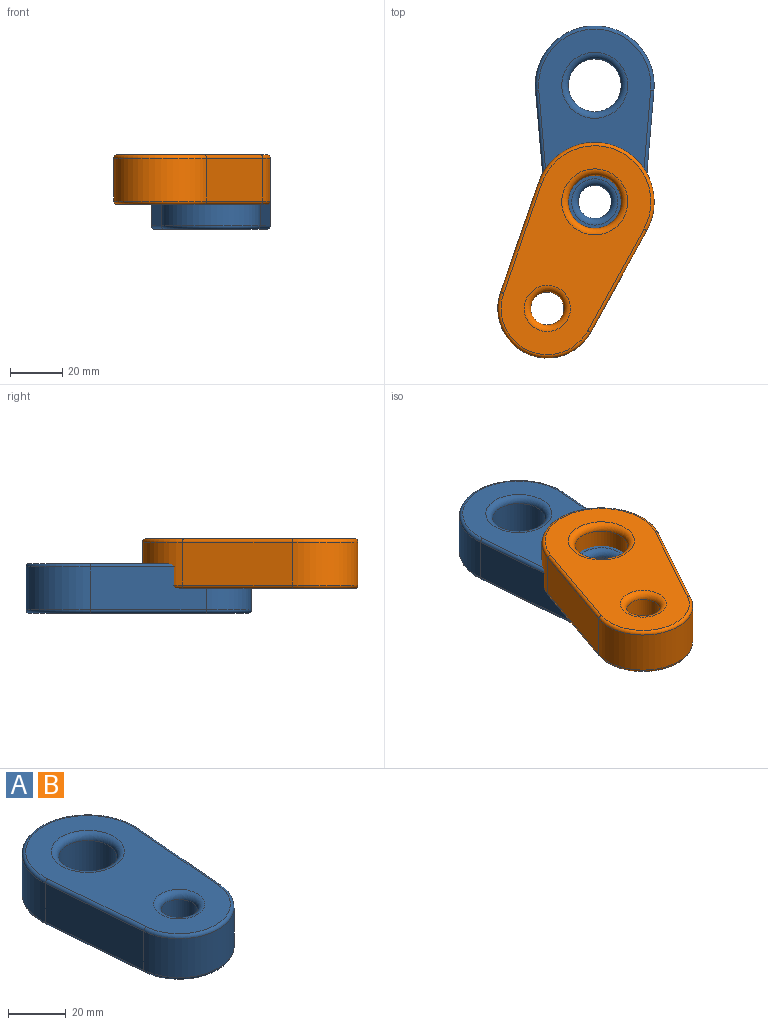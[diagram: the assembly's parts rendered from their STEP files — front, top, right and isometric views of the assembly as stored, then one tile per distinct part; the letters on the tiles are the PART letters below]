
ASSEMBLY  parts=2 mates=1
PART A: 20 faces, bbox 49.5x90.2x19.1 mm
  f0: cylinder r=19.05mm len=37.96mm, axis (0,0,-1), area 934.6mm2, adj f1,f3,f14,f18
  f1: plane 44.53x16.51mm, normal (1,-0.08,0), area 737.8mm2, adj f0,f2,f15,f19
  f2: cylinder r=22.86mm len=45.72mm, axis (0,0,-1), area 1249.9mm2, adj f1,f3,f13,f17
  f3: plane 44.53x16.51mm, normal (-1,-0.08,0), area 737.8mm2, adj f0,f2,f12,f16
  f4: cylinder r=6.35mm len=13.97mm, axis (0,0,-1), area 557.4mm2, adj f9,f11
  f5: cylinder r=10.16mm len=20.32mm, axis (0,0,-1), area 891.8mm2, adj f8,f10
  f6: plane 84.22x43.18mm, normal (0,0,1), area 2245.9mm2, adj f10,f11,f16,f17,f18,f19
  f7: plane 84.22x43.18mm, normal (0,0,-1), area 2245.9mm2, adj f8,f9,f12,f13,f14,f15
  f8: torus R=12.7mm, axis (0,0,1), area 277.8mm2, adj f5,f7
  f9: torus R=8.89mm, axis (0,0,1), area 182.3mm2, adj f4,f7
  f10: torus R=12.7mm, axis (0,0,1), area 277.8mm2, adj f5,f6
  f11: torus R=8.89mm, axis (0,0,1), area 182.3mm2, adj f4,f6
  f12: cylinder r=1.27mm len=44.63mm, axis (0.08,-1,0), area 89.1mm2, adj f3,f7,f13,f14
  f13: torus R=21.59mm, axis (0,0,1), area 148mm2, adj f2,f7,f12,f15
  f14: torus R=17.78mm, axis (0,0,1), area 110.2mm2, adj f0,f7,f12,f15
  f15: cylinder r=1.27mm len=44.63mm, axis (0.08,1,0), area 89.1mm2, adj f1,f7,f13,f14
  f16: cylinder r=1.27mm len=44.63mm, axis (-0.08,1,0), area 89.1mm2, adj f3,f6,f17,f18
  f17: torus R=21.59mm, axis (0,0,1), area 148mm2, adj f2,f6,f16,f19
  f18: torus R=17.78mm, axis (0,0,1), area 110.2mm2, adj f0,f6,f16,f19
  f19: cylinder r=1.27mm len=44.63mm, axis (-0.08,-1,0), area 89.1mm2, adj f1,f6,f17,f18
PART B: same geometry as A
PLACE A t=(5.2,23.36,-4.45)mm fixed
PLACE B rot(axis=(0,0,-1),24deg) t=(2.39,-16.97,5.07)mm
MATE revolute B.f2 <-> A.f0  axis (0,0,-1) through (14.44,-12.62,14.6)mm
